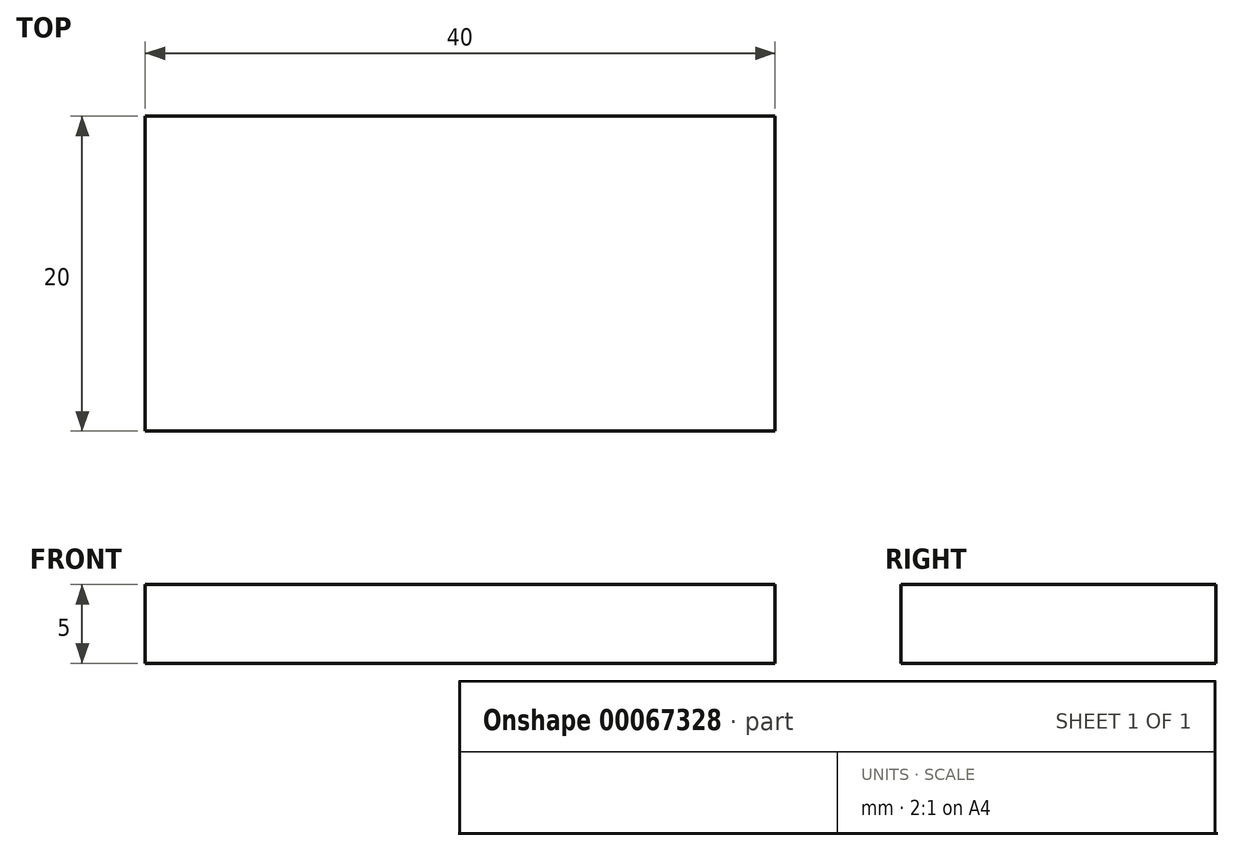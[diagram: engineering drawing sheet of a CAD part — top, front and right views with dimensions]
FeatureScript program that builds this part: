
annotation { "Feature Type Name" : "Feature", "Feature Type Description" : "" }
export const myFeature = defineFeature(function(context is Context, id is Id, definition is map)
    precondition{}
    {
        {
            var Q0;
            Q0=qCreatedBy(makeId("Top.planeOp"),FACE);
            var sketch = newSketch(context, id + "F0", { "sketchPlane" : qUnion([Q0])});
            skLineSegment(sketch, "E0.bottom", {"start": v(0, 0) * mm, "end": v(40, 0) * mm});
            skLineSegment(sketch, "E0.top", {"start": v(0, 20) * mm, "end": v(40, 20) * mm});
            skLineSegment(sketch, "E0.left", {"start": v(0, 0) * mm, "end": v(0, 20) * mm});
            skLineSegment(sketch, "E0.right", {"start": v(40, 0) * mm, "end": v(40, 20) * mm});
            skSolve(sketch);
        }
        {
            var Q0;
            Q0=makeQuery(id+"F0.imprint","IMPRINT",FACE,{"disambiguationData":[TD([[makeQuery(id+"F0.imprint","IMPRINT",EDGE,{"derivedFrom":sQuery(id+"F0.wireOp",EDGE,"E0.bottom")}),1.0]])]});
            extrude(context, id + "F1", {"entities" : qUnion([Q0]), "depth" : 5 * mm});
        }
    });
